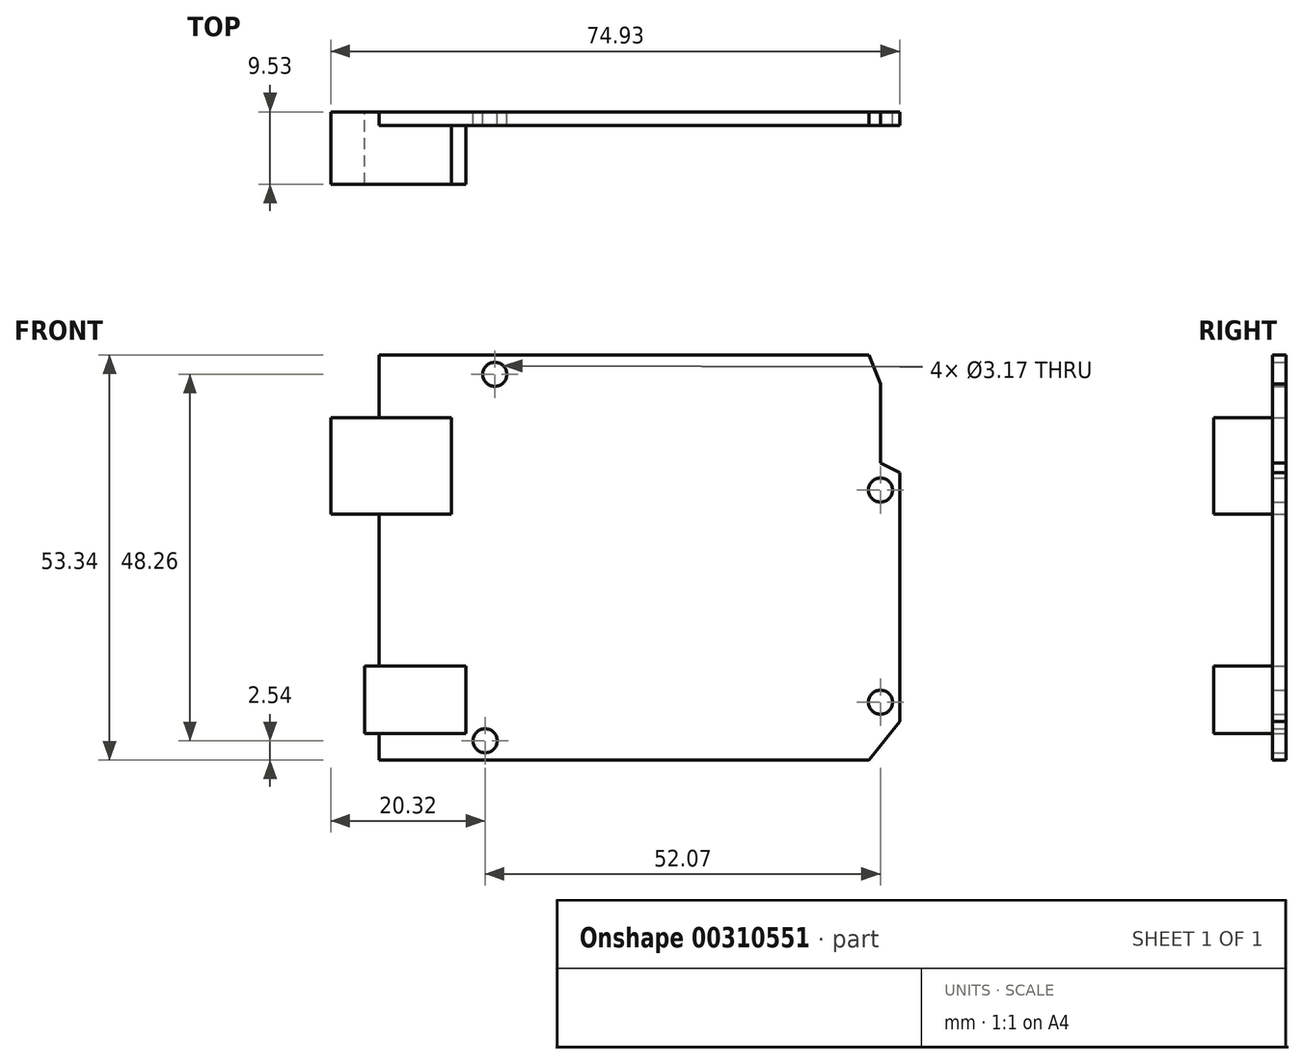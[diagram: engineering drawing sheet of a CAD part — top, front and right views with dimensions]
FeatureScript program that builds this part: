
annotation { "Feature Type Name" : "Feature", "Feature Type Description" : "" }
export const myFeature = defineFeature(function(context is Context, id is Id, definition is map)
    precondition{}
    {
        {
            var Q0;
            Q0=qCreatedBy(makeId("Front.planeOp"),FACE);
            var sketch = newSketch(context, id + "F0", { "sketchPlane" : qUnion([Q0])});
            skLineSegment(sketch, "E0", {"start": v(0, 0) * mm, "end": v(64.52, 0) * mm});
            skLineSegment(sketch, "E1", {"start": v(0, 0) * mm, "end": v(0, 0.32) * mm});
            skLineSegment(sketch, "E2", {"start": v(0, 53.34) * mm, "end": v(64.52, 53.34) * mm});
            skLineSegment(sketch, "E3", {"start": v(64.52, 53.34) * mm, "end": v(66.04, 49.56) * mm});
            skLineSegment(sketch, "E4", {"start": v(64.52, 0) * mm, "end": v(68.58, 5.08) * mm});
            skLineSegment(sketch, "E5", {"start": v(68.58, 5.08) * mm, "end": v(68.58, 37.85) * mm});
            skLineSegment(sketch, "E6", {"start": v(66.04, 49.56) * mm, "end": v(66.04, 39.15) * mm});
            skLineSegment(sketch, "E7", {"start": v(66.04, 39.15) * mm, "end": v(68.58, 37.85) * mm});
            skPoint(sketch, "E8.end.orphan", {"position": v(68.58, 23) * mm});
            skLineSegment(sketch, "E9", {"start": v(9.53, 32.38) * mm, "end": v(9.53, 45.09) * mm});
            skLineSegment(sketch, "E10", {"start": v(9.53, 45.09) * mm, "end": v(-6.35, 45.09) * mm});
            skLineSegment(sketch, "E11", {"start": v(-6.35, 45.09) * mm, "end": v(-6.35, 32.38) * mm});
            skLineSegment(sketch, "E12", {"start": v(-6.35, 32.38) * mm, "end": v(9.53, 32.38) * mm});
            skCircle(sketch, "E13", {"center": v(13.97, 2.54) * mm, "radius": 1.59 * mm});
            skCircle(sketch, "E14", {"center": v(15.24, 50.8) * mm, "radius": 1.59 * mm});
            skCircle(sketch, "E15", {"center": v(66.04, 7.62) * mm, "radius": 1.59 * mm});
            skCircle(sketch, "E16", {"center": v(66.04, 35.56) * mm, "radius": 1.59 * mm});
            skPoint(sketch, "E17.start.orphan", {"position": v(32.26, 0) * mm});
            skLineSegment(sketch, "E18.trimOffspring", {"start": v(0, 9.2) * mm, "end": v(0, 32.38) * mm});
            skLineSegment(sketch, "E19.trimOffspring", {"start": v(0, 45.09) * mm, "end": v(0, 53.34) * mm});
            skLineSegment(sketch, "E20", {"start": v(-27.95, 0.32) * mm, "end": v(-27.95, 3.5) * mm});
            skLineSegment(sketch, "E21", {"start": v(0, -11.36) * mm, "end": v(-1.9, -11.36) * mm});
            skLineSegment(sketch, "E22", {"start": v(-1.9, 3.5) * mm, "end": v(-1.9, 12.38) * mm});
            skLineSegment(sketch, "E23", {"start": v(-1.9, 12.38) * mm, "end": v(11.43, 12.38) * mm});
            skLineSegment(sketch, "E24", {"start": v(11.43, 12.38) * mm, "end": v(11.43, 3.5) * mm});
            skLineSegment(sketch, "E25", {"start": v(11.43, 3.5) * mm, "end": v(-1.9, 3.5) * mm});
            skLineSegment(sketch, "E26", {"start": v(0, 0.32) * mm, "end": v(0, 3.5) * mm});
            skSolve(sketch);
        }
        {
            var Q0;
            Q0=makeQuery(id+"F0.imprint","IMPRINT",FACE,{"disambiguationData":[TD([[makeQuery(id+"F0.imprint","IMPRINT",EDGE,{"derivedFrom":sQuery(id+"F0.wireOp",EDGE,"E0")}),1.0]])]});
            extrude(context, id + "F1", {"entities" : qUnion([Q0]), "depth" : 1.78 * mm});
        }
        {
            var Q0;
            {var subQ3=sQuery(id+"F0.wireOp",EDGE,"E22");Q0=makeQuery(id+"F0.imprint","IMPRINT",FACE,{"disambiguationData":[TD([[makeQuery(id+"F0.imprint","IMPRINT",EDGE,{"derivedFrom":subQ3}),-1.0]])]});}
            var Q1;
            {var subQ3=sQuery(id+"F0.wireOp",EDGE,"E9");Q1=makeQuery(id+"F0.imprint","IMPRINT",FACE,{"disambiguationData":[TD([[makeQuery(id+"F0.imprint","IMPRINT",EDGE,{"derivedFrom":subQ3}),1.0]])]});}
            extrude(context, id + "F2", {"entities" : qUnion([Q0, Q1]), "operationType" : NewBodyOperationType.ADD, "depth" : 9.52 * mm});
        }
    });
